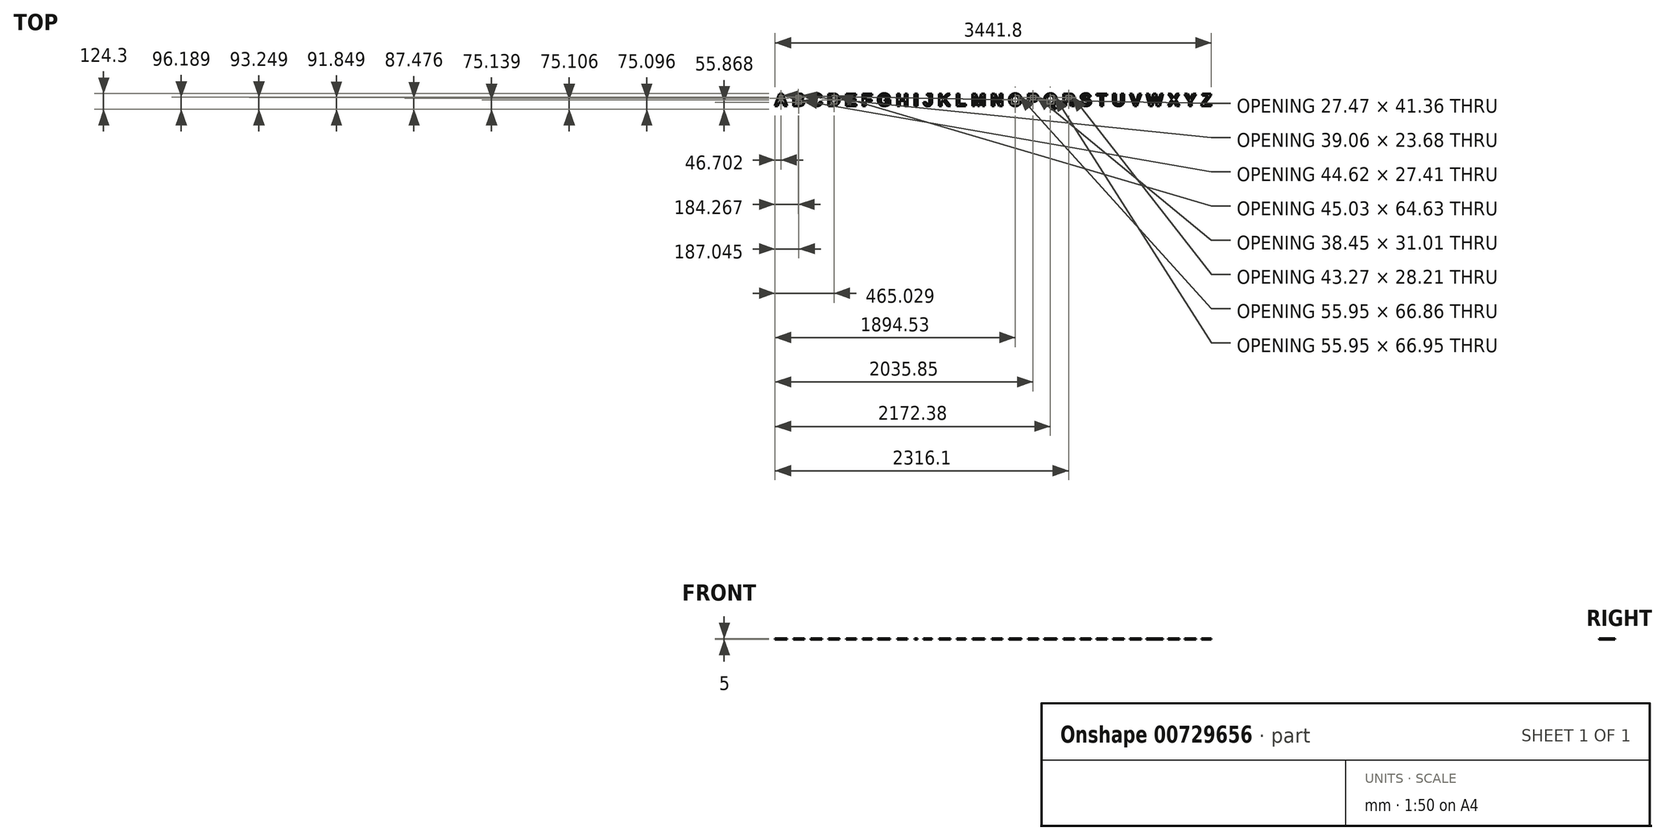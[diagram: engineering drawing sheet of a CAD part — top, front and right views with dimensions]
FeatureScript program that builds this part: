
annotation { "Feature Type Name" : "Feature", "Feature Type Description" : "" }
export const myFeature = defineFeature(function(context is Context, id is Id, definition is map)
    precondition{}
    {
        {
            var Q0;
            Q0=qCreatedBy(makeId("Top.planeOp"), FACE);
            var sketch = newSketch(context, id + "F0", { "sketchPlane" : qUnion([Q0])});
            skText(sketch, "E0", { "text": "A B C D E F G H I J K L M N O P Q R S T U V W X Y Z", "fontName": "Arimo-Bold.ttf"});
            const initialGuessF0  = {"E0": [0, 0, 1, 0, 0.1]};
            skSetInitialGuess(sketch, initialGuessF0);
            skSolve(sketch);
        }
        {
            var Q0;
            Q0 = qSketchRegion(id + "F0", true);
            extrude(context, id + "F1", {"entities" : qUnion([Q0]), "depth" : 5 * mm, "offsetDistance" : 25 * mm});
        }
    });
